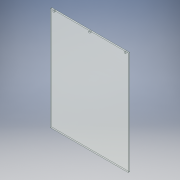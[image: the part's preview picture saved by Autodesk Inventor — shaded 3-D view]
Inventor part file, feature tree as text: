
AUTODESK INVENTOR PART (.ipt)
format: ipt  version: 2019 (Build 230136000, 136)  size: 111,616 bytes
history: native  units: mm
features: extrude x2, sketch x2
ambient origin geometry x8: Origin, YZ Plane, XZ Plane, XY Plane, X Axis, Y Axis, Z Axis, Center Point
bodies: Solid1 (feature_tree)
feature tree (4):
  extrude  "Extrusion1"  Depth=300.0mm
  extrude  "Extrusion2"  Depth=10.0mm
  sketch  "Sketch1"  dims[d0=400.0mm d1=300.0mm]
  sketch  "Sketch3"  dims[d2=142.857143mm d3=200.0mm d4=5.0mm d5=0.0mm d6=7.0mm d7=7.0mm d8=7.0mm d9=12.0mm d10=12.0mm d11=150.0mm d12=5.0mm d13=5.0mm d14=5.0mm d15=10.0mm d16=0.0mm]
